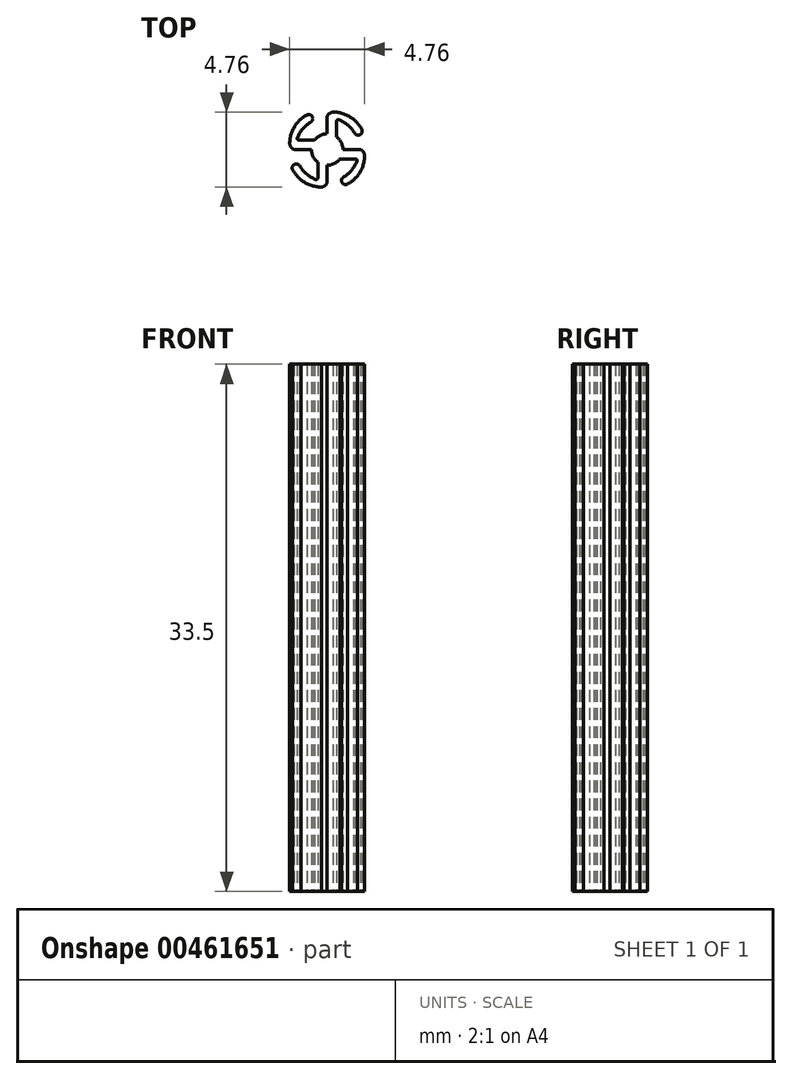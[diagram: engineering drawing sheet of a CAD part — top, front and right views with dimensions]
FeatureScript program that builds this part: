
annotation { "Feature Type Name" : "Feature", "Feature Type Description" : "" }
export const myFeature = defineFeature(function(context is Context, id is Id, definition is map)
    precondition{}
    {
        {
            var Q0;
            Q0=qCreatedBy(makeId("Top.planeOp"),FACE);
            var sketch = newSketch(context, id + "F0", { "sketchPlane" : qUnion([Q0])});
            skArc(sketch, "E0", {"start": v(31.06, -20.61) * mm, "mid": v(31.17, -21.06) * mm, "end": v(31.46, -21.41) * mm});
            skLineSegment(sketch, "E1", {"start": v(32.06, -19.61) * mm, "end": v(32.06, -18.5) * mm});
            skArc(sketch, "E2", {"start": v(33.83, -19.61) * mm, "mid": v(33.39, -19.07) * mm, "end": v(32.8, -18.72) * mm});
            skLineSegment(sketch, "E3", {"start": v(32.66, -19.8) * mm, "end": v(32.66, -18.8) * mm});
            skPoint(sketch, "E4", {"position": v(32.06, -18.26) * mm});
            skArc(sketch, "E5", {"start": v(33.78, -19.53) * mm, "mid": v(34.14, -19.67) * mm, "end": v(34.24, -19.29) * mm});
            skArc(sketch, "E6", {"start": v(33.73, -18.69) * mm, "mid": v(33.11, -18.35) * mm, "end": v(32.42, -18.23) * mm});
            skArc(sketch, "E7.trimOffspring", {"start": v(34.26, -19.32) * mm, "mid": v(34.02, -18.98) * mm, "end": v(33.73, -18.69) * mm});
            skArc(sketch, "E8", {"start": v(32.42, -18.23) * mm, "mid": v(32.2, -18.32) * mm, "end": v(32.06, -18.5) * mm});
            skPoint(sketch, "E9.visualSharp", {"position": v(32.66, -18.67) * mm});
            skArc(sketch, "E9.filletArc", {"start": v(32.8, -18.72) * mm, "mid": v(32.7, -18.73) * mm, "end": v(32.66, -18.8) * mm});
            skLineSegment(sketch, "E10.1.0", {"start": v(31.06, -20.61) * mm, "end": v(29.95, -20.61) * mm});
            skArc(sketch, "E10.1.1", {"start": v(29.68, -20.25) * mm, "mid": v(29.76, -20.47) * mm, "end": v(29.95, -20.61) * mm});
            skArc(sketch, "E10.1.2", {"start": v(30.13, -18.94) * mm, "mid": v(29.8, -19.56) * mm, "end": v(29.68, -20.25) * mm});
            skArc(sketch, "E10.1.3", {"start": v(30.76, -18.41) * mm, "mid": v(30.43, -18.65) * mm, "end": v(30.13, -18.94) * mm});
            skArc(sketch, "E10.1.4", {"start": v(30.98, -18.9) * mm, "mid": v(31.12, -18.53) * mm, "end": v(30.74, -18.43) * mm});
            skArc(sketch, "E10.1.5", {"start": v(31.06, -18.84) * mm, "mid": v(30.52, -19.28) * mm, "end": v(30.16, -19.88) * mm});
            skLineSegment(sketch, "E10.1.6", {"start": v(31.26, -20.01) * mm, "end": v(30.26, -20.01) * mm});
            skArc(sketch, "E10.1.7", {"start": v(30.16, -19.88) * mm, "mid": v(30.18, -19.97) * mm, "end": v(30.26, -20.01) * mm});
            skLineSegment(sketch, "E10.2.0", {"start": v(32.06, -21.61) * mm, "end": v(32.06, -22.72) * mm});
            skArc(sketch, "E10.2.1", {"start": v(31.7, -23) * mm, "mid": v(31.91, -22.9) * mm, "end": v(32.06, -22.72) * mm});
            skArc(sketch, "E10.2.2", {"start": v(30.39, -22.54) * mm, "mid": v(31, -22.87) * mm, "end": v(31.7, -23) * mm});
            skArc(sketch, "E10.2.3", {"start": v(29.86, -21.9) * mm, "mid": v(30.1, -22.24) * mm, "end": v(30.39, -22.54) * mm});
            skArc(sketch, "E10.2.4", {"start": v(30.34, -21.7) * mm, "mid": v(29.97, -21.55) * mm, "end": v(29.88, -21.93) * mm});
            skArc(sketch, "E10.2.5", {"start": v(30.3, -21.61) * mm, "mid": v(30.73, -22.15) * mm, "end": v(31.33, -22.5) * mm});
            skLineSegment(sketch, "E10.2.6", {"start": v(31.46, -21.41) * mm, "end": v(31.46, -22.41) * mm});
            skArc(sketch, "E10.2.7", {"start": v(31.33, -22.5) * mm, "mid": v(31.42, -22.5) * mm, "end": v(31.46, -22.41) * mm});
            skLineSegment(sketch, "E10.3.0", {"start": v(33.06, -20.61) * mm, "end": v(34.17, -20.61) * mm});
            skArc(sketch, "E10.3.1", {"start": v(34.44, -20.97) * mm, "mid": v(34.36, -20.76) * mm, "end": v(34.17, -20.61) * mm});
            skArc(sketch, "E10.3.2", {"start": v(33.98, -22.28) * mm, "mid": v(34.32, -21.67) * mm, "end": v(34.44, -20.97) * mm});
            skArc(sketch, "E10.3.3", {"start": v(33.35, -22.8) * mm, "mid": v(33.7, -22.57) * mm, "end": v(33.98, -22.28) * mm});
            skArc(sketch, "E10.3.4", {"start": v(33.14, -22.33) * mm, "mid": v(33, -22.7) * mm, "end": v(33.38, -22.8) * mm});
            skArc(sketch, "E10.3.5", {"start": v(33.06, -22.38) * mm, "mid": v(33.6, -21.94) * mm, "end": v(33.95, -21.34) * mm});
            skLineSegment(sketch, "E10.3.6", {"start": v(32.86, -21.2) * mm, "end": v(33.86, -21.2) * mm});
            skArc(sketch, "E10.3.7", {"start": v(33.95, -21.34) * mm, "mid": v(33.94, -21.25) * mm, "end": v(33.86, -21.2) * mm});
            skArc(sketch, "E11.trimOffspring", {"start": v(32.06, -19.61) * mm, "mid": v(31.61, -19.72) * mm, "end": v(31.26, -20.01) * mm});
            skArc(sketch, "E12.trimOffspring", {"start": v(33.06, -20.61) * mm, "mid": v(32.95, -20.16) * mm, "end": v(32.66, -19.8) * mm});
            skArc(sketch, "E13.trimOffspring", {"start": v(32.06, -21.61) * mm, "mid": v(32.5, -21.5) * mm, "end": v(32.86, -21.2) * mm});
            skSolve(sketch);
        }
        {
            var Q0;
            Q0=makeQuery(id+"F0.imprint","IMPRINT",FACE,{"disambiguationData":[TD([[makeQuery(id+"F0.imprint","IMPRINT",EDGE,{"derivedFrom":sQuery(id+"F0.wireOp",EDGE,"E0")}),1.0]])]});
            extrude(context, id + "F1", {"entities" : qUnion([Q0]), "depth" : 33.5 * mm});
        }
    });
